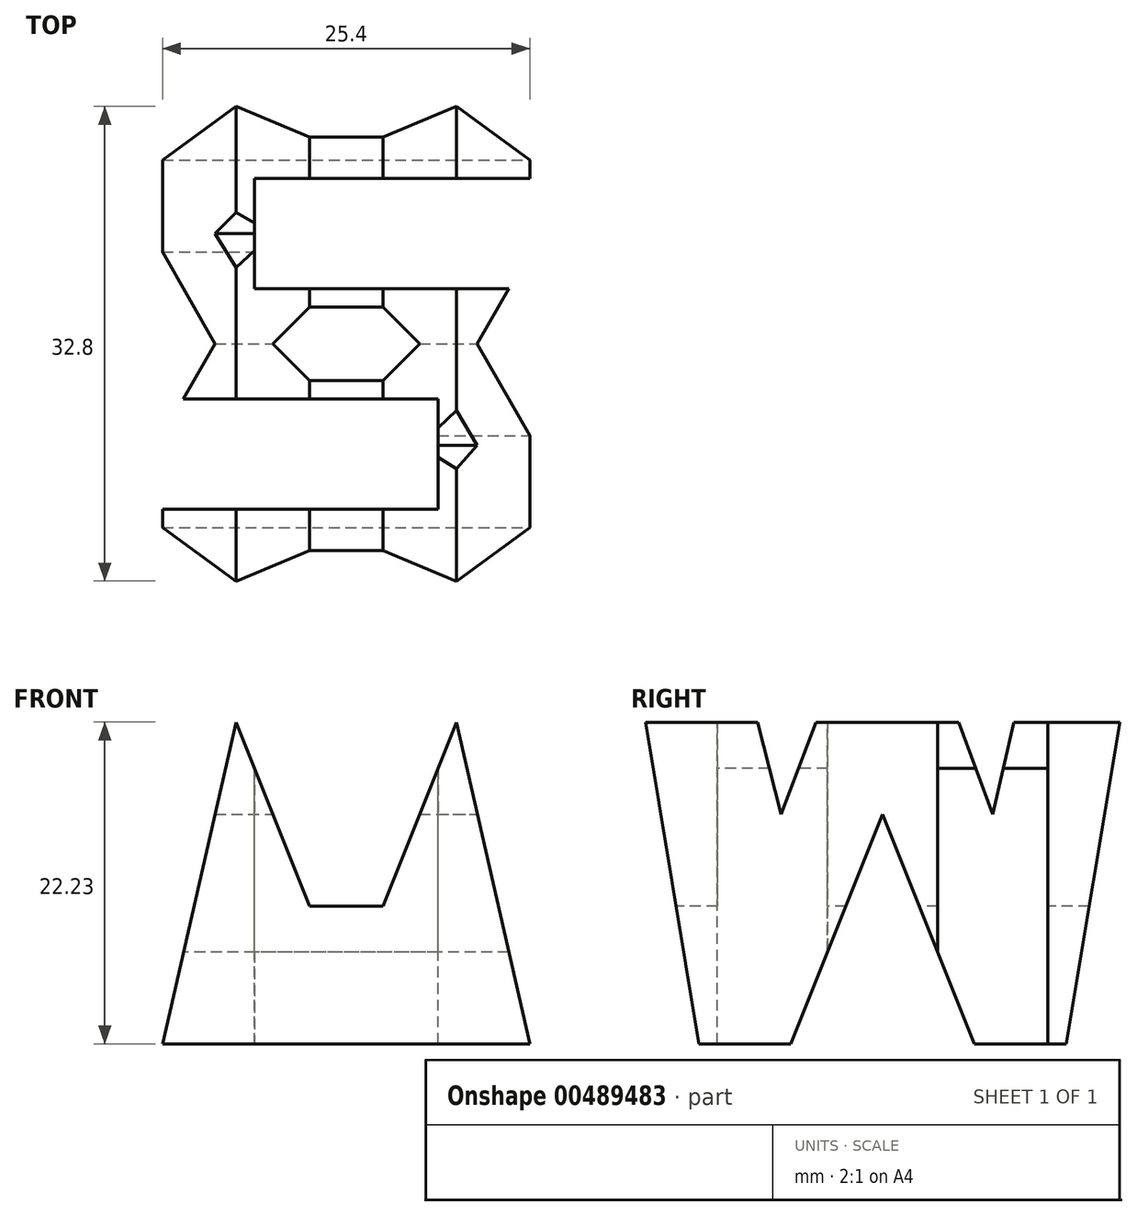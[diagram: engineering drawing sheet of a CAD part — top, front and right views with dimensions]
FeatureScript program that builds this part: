
annotation { "Feature Type Name" : "Feature", "Feature Type Description" : "" }
export const myFeature = defineFeature(function(context is Context, id is Id, definition is map)
    precondition{}
    {
        {
            var Q0;
            Q0=qCreatedBy(makeId("Front.planeOp"),FACE);
            var sketch = newSketch(context, id + "F0", { "sketchPlane" : qUnion([Q0])});
            skLineSegment(sketch, "E0", {"start": v(0, 0) * mm, "end": v(38.1, 0) * mm});
            skLineSegment(sketch, "E1", {"start": v(38.1, 0) * mm, "end": v(38.1, 38.1) * mm});
            skLineSegment(sketch, "E2", {"start": v(38.1, 38.1) * mm, "end": v(0, 38.1) * mm});
            skLineSegment(sketch, "E3", {"start": v(0, 38.1) * mm, "end": v(0, 0) * mm});
            skSolve(sketch);
        }
        {
            var Q0;
            Q0=makeQuery(id+"F0.imprint","IMPRINT",FACE,{"disambiguationData":[TD([[makeQuery(id+"F0.imprint","IMPRINT",EDGE,{"derivedFrom":sQuery(id+"F0.wireOp",EDGE,"E0")}),1.0]])]});
            extrude(context, id + "F1", {"entities" : qUnion([Q0]), "depth" : 38.1 * mm, "offsetDistance" : 25.4 * mm});
        }
        {
            var Q0;
            Q0=qCreatedBy(makeId("Front.planeOp"),FACE);
            cPlane(context, id + "F2", {"entities" : qUnion([Q0]), "cplaneType" : CPlaneType.OFFSET, "offset" : 38.1 * mm, "width" : 152.4 * mm, "height" : 152.4 * mm});
        }
        {
            var Q0;
            Q0=qCreatedBy(makeId("Right.planeOp"),FACE);
            cPlane(context, id + "F3", {"entities" : qUnion([Q0]), "cplaneType" : CPlaneType.OFFSET, "offset" : 38.1 * mm, "width" : 152.4 * mm, "height" : 152.4 * mm});
        }
        {
            var Q0;
            Q0=qCreatedBy(makeId("Top.planeOp"),FACE);
            cPlane(context, id + "F4", {"entities" : qUnion([Q0]), "cplaneType" : CPlaneType.OFFSET, "offset" : 38.1 * mm, "width" : 152.4 * mm, "height" : 152.4 * mm});
        }
        {
            var Q0;
            Q0=qCreatedBy(id+"F3.planeOp",FACE);
            var sketch = newSketch(context, id + "F5", { "sketchPlane" : qUnion([Q0])});
            skLineSegment(sketch, "E4", {"start": v(-38.1, 38.1) * mm, "end": v(-31.75, 38.1) * mm});
            skLineSegment(sketch, "E5", {"start": v(-38.1, 38.1) * mm, "end": v(-31.75, 0) * mm});
            skLineSegment(sketch, "E6", {"start": v(-31.75, 0) * mm, "end": v(-25.4, 0) * mm});
            skLineSegment(sketch, "E7", {"start": v(0, 38.1) * mm, "end": v(-6.35, 38.1) * mm});
            skLineSegment(sketch, "E8", {"start": v(0, 38.1) * mm, "end": v(-6.35, 0) * mm});
            skLineSegment(sketch, "E9", {"start": v(-6.35, 0) * mm, "end": v(-12.7, 0) * mm});
            skLineSegment(sketch, "E10", {"start": v(-11.43, 15.88) * mm, "end": v(-6.35, 38.1) * mm});
            skLineSegment(sketch, "E11", {"start": v(-25.4, 0) * mm, "end": v(-19.05, 15.88) * mm});
            skLineSegment(sketch, "E12", {"start": v(-19.05, 15.88) * mm, "end": v(-12.7, 0) * mm});
            skLineSegment(sketch, "E13", {"start": v(-26.08, 15.88) * mm, "end": v(-21.24, 28.58) * mm});
            skLineSegment(sketch, "E14", {"start": v(-21.24, 28.58) * mm, "end": v(-16.16, 28.58) * mm});
            skLineSegment(sketch, "E15", {"start": v(-16.16, 28.58) * mm, "end": v(-11.43, 15.88) * mm});
            skLineSegment(sketch, "E16", {"start": v(-31.75, 38.1) * mm, "end": v(-26.08, 15.87) * mm});
            skLineSegment(sketch, "E17.bottom", {"start": v(0, 0) * mm, "end": v(-38.1, 0) * mm});
            skLineSegment(sketch, "E17.top", {"start": v(0, 38.1) * mm, "end": v(-38.1, 38.1) * mm});
            skLineSegment(sketch, "E17.left", {"start": v(0, 0) * mm, "end": v(0, 38.1) * mm});
            skLineSegment(sketch, "E17.right", {"start": v(-38.1, 0) * mm, "end": v(-38.1, 38.1) * mm});
            skSolve(sketch);
        }
        {
            var Q0;
            {var subQ0=sQuery(id+"F5.wireOp",EDGE,"E10");Q0=makeQuery(id+"F5.imprint","IMPRINT",FACE,{"disambiguationData":[TD([[makeQuery(id+"F5.imprint","IMPRINT",EDGE,{"derivedFrom":subQ0}),1.0]])]});}
            var Q1;
            {var subQ0=sQuery(id+"F5.wireOp",EDGE,"E11");Q1=makeQuery(id+"F5.imprint","IMPRINT",FACE,{"disambiguationData":[TD([[makeQuery(id+"F5.imprint","IMPRINT",EDGE,{"derivedFrom":subQ0}),-1.0]])]});}
            var Q2;
            {var subQ0=sQuery(id+"F5.wireOp",EDGE,"E8");Q2=makeQuery(id+"F5.imprint","IMPRINT",FACE,{"disambiguationData":[TD([[makeQuery(id+"F5.imprint","IMPRINT",EDGE,{"derivedFrom":subQ0}),1.0]])]});}
            var Q3;
            {var subQ0=sQuery(id+"F5.wireOp",EDGE,"E5");Q3=makeQuery(id+"F5.imprint","IMPRINT",FACE,{"disambiguationData":[TD([[makeQuery(id+"F5.imprint","IMPRINT",EDGE,{"derivedFrom":subQ0}),-1.0]])]});}
            extrude(context, id + "F6", {"entities" : qUnion([Q0, Q1, Q2, Q3]), "operationType" : NewBodyOperationType.REMOVE, "oppositeDirection" : true, "depth" : 38.1 * mm, "offsetDistance" : 25.4 * mm});
        }
        {
            var Q0;
            Q0=qCreatedBy(id+"F2.planeOp",FACE);
            var sketch = newSketch(context, id + "F7", { "sketchPlane" : qUnion([Q0])});
            skLineSegment(sketch, "E18", {"start": v(0, 0) * mm, "end": v(38.1, 0) * mm});
            skLineSegment(sketch, "E19", {"start": v(38.1, 0) * mm, "end": v(38.1, 38.1) * mm});
            skLineSegment(sketch, "E20", {"start": v(38.1, 38.1) * mm, "end": v(0, 38.1) * mm});
            skLineSegment(sketch, "E21", {"start": v(0, 38.1) * mm, "end": v(0, 0) * mm});
            skLineSegment(sketch, "E22", {"start": v(6.35, 38.1) * mm, "end": v(0, 0) * mm});
            skLineSegment(sketch, "E23", {"start": v(6.35, 38.1) * mm, "end": v(12.7, 38.1) * mm});
            skLineSegment(sketch, "E24", {"start": v(12.7, 38.1) * mm, "end": v(19.05, 22.23) * mm});
            skLineSegment(sketch, "E25", {"start": v(19.05, 22.23) * mm, "end": v(25.4, 38.1) * mm});
            skLineSegment(sketch, "E26", {"start": v(25.4, 38.1) * mm, "end": v(31.75, 38.1) * mm});
            skLineSegment(sketch, "E27", {"start": v(31.75, 38.1) * mm, "end": v(38.1, 0) * mm});
            skLineSegment(sketch, "E28", {"start": v(38.1, 0) * mm, "end": v(31.75, 0) * mm});
            skLineSegment(sketch, "E29", {"start": v(0, 0) * mm, "end": v(6.35, 0) * mm});
            skLineSegment(sketch, "E30", {"start": v(6.35, 0) * mm, "end": v(11.43, 22.23) * mm});
            skLineSegment(sketch, "E31", {"start": v(31.75, 0) * mm, "end": v(26.67, 22.23) * mm});
            skLineSegment(sketch, "E32", {"start": v(26.67, 22.23) * mm, "end": v(21.6, 9.52) * mm});
            skLineSegment(sketch, "E33", {"start": v(11.43, 22.23) * mm, "end": v(16.51, 9.53) * mm});
            skLineSegment(sketch, "E34", {"start": v(16.51, 9.52) * mm, "end": v(21.59, 9.52) * mm});
            skSolve(sketch);
        }
        {
            var Q0;
            {var subQ0=sQuery(id+"F7.wireOp",EDGE,"E24");Q0=makeQuery(id+"F7.imprint","IMPRINT",FACE,{"disambiguationData":[TD([[makeQuery(id+"F7.imprint","IMPRINT",EDGE,{"derivedFrom":subQ0}),1.0]])]});}
            var Q1;
            {var subQ0=sQuery(id+"F7.wireOp",EDGE,"E21");Q1=makeQuery(id+"F7.imprint","IMPRINT",FACE,{"disambiguationData":[TD([[makeQuery(id+"F7.imprint","IMPRINT",EDGE,{"derivedFrom":subQ0}),1.0]])]});}
            var Q2;
            Q2=makeQuery(id+"F7.imprint","IMPRINT",FACE,{"disambiguationData":[TD([[makeQuery(id+"F7.imprint","IMPRINT",EDGE,{"derivedFrom":sQuery(id+"F7.wireOp",EDGE,"E18")}),1.0]])]});
            var Q3;
            {var subQ0=sQuery(id+"F7.wireOp",EDGE,"E19");Q3=makeQuery(id+"F7.imprint","IMPRINT",FACE,{"disambiguationData":[TD([[makeQuery(id+"F7.imprint","IMPRINT",EDGE,{"derivedFrom":subQ0}),1.0]])]});}
            extrude(context, id + "F8", {"entities" : qUnion([Q0, Q1, Q2, Q3]), "operationType" : NewBodyOperationType.REMOVE, "oppositeDirection" : true, "depth" : 38.1 * mm, "offsetDistance" : 25.4 * mm});
        }
        {
            var Q0;
            Q0=qCreatedBy(id+"F4.planeOp",FACE);
            var sketch = newSketch(context, id + "F9", { "sketchPlane" : qUnion([Q0])});
            skLineSegment(sketch, "E35", {"start": v(0, 0) * mm, "end": v(38.1, 0) * mm});
            skLineSegment(sketch, "E36", {"start": v(38.1, 0) * mm, "end": v(38.1, -38.1) * mm});
            skLineSegment(sketch, "E37", {"start": v(38.1, -38.1) * mm, "end": v(0, -38.1) * mm});
            skLineSegment(sketch, "E38", {"start": v(0, -38.1) * mm, "end": v(0, 0) * mm});
            skLineSegment(sketch, "E39", {"start": v(38.1, -7.62) * mm, "end": v(12.7, -7.62) * mm});
            skLineSegment(sketch, "E40", {"start": v(12.7, -7.62) * mm, "end": v(12.7, -15.24) * mm});
            skLineSegment(sketch, "E41", {"start": v(12.7, -15.24) * mm, "end": v(38.1, -15.24) * mm});
            skLineSegment(sketch, "E42", {"start": v(0, -22.86) * mm, "end": v(25.4, -22.86) * mm});
            skLineSegment(sketch, "E43", {"start": v(25.4, -22.86) * mm, "end": v(25.4, -30.48) * mm});
            skLineSegment(sketch, "E44", {"start": v(25.4, -30.48) * mm, "end": v(0, -30.48) * mm});
            skSolve(sketch);
        }
        {
            var Q0;
            {var subQ0=sQuery(id+"F9.wireOp",EDGE,"E39");Q0=makeQuery(id+"F9.imprint","IMPRINT",FACE,{"disambiguationData":[TD([[makeQuery(id+"F9.imprint","IMPRINT",EDGE,{"derivedFrom":subQ0}),1.0]])]});}
            var Q1;
            {var subQ0=sQuery(id+"F9.wireOp",EDGE,"E42");Q1=makeQuery(id+"F9.imprint","IMPRINT",FACE,{"disambiguationData":[TD([[makeQuery(id+"F9.imprint","IMPRINT",EDGE,{"derivedFrom":subQ0}),-1.0]])]});}
            extrude(context, id + "F10", {"entities" : qUnion([Q0, Q1]), "operationType" : NewBodyOperationType.REMOVE, "oppositeDirection" : true, "depth" : 38.1 * mm, "offsetDistance" : 25.4 * mm});
        }
    });
